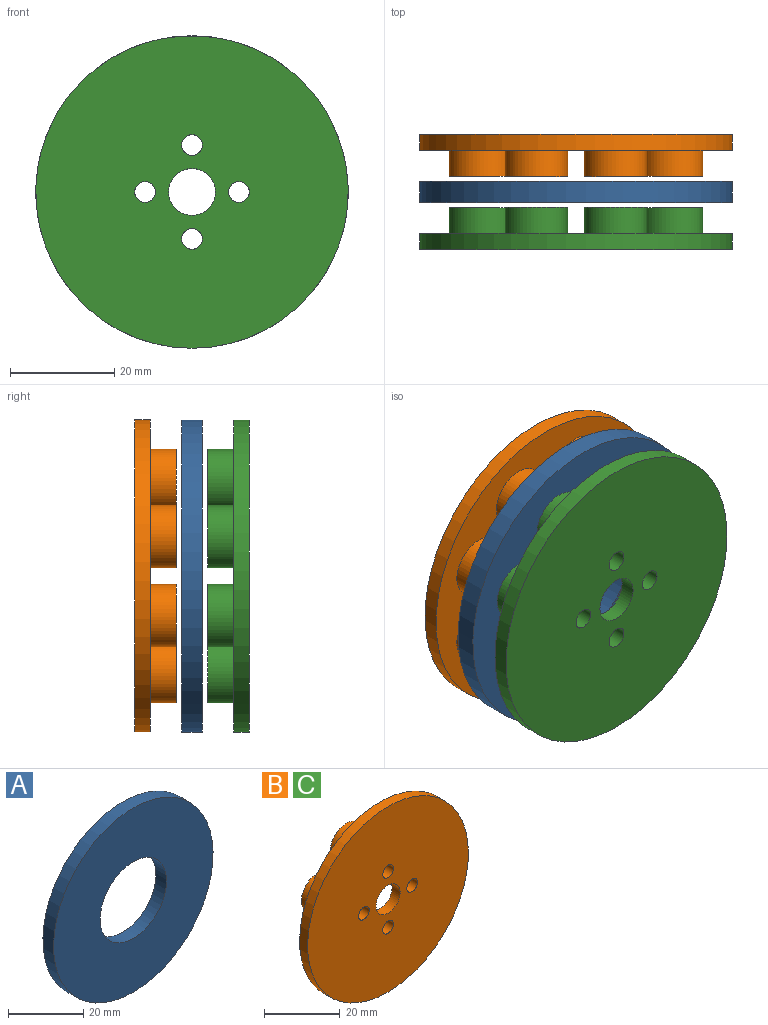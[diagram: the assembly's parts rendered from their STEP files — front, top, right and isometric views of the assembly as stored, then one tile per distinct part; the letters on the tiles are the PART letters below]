
ASSEMBLY  parts=3 mates=4
PART A: 4 faces, bbox 60x4x60 mm
  f0: cylinder r=12.5mm len=25mm, axis (0,1,0), area 314.2mm2, adj f2,f3
  f1: cylinder r=30mm len=60mm, axis (0,1,0), area 754mm2, adj f2,f3
  f2: plane 60x60mm, normal (0,-1,0), area 2336.6mm2, adj f0,f1
  f3: plane 60x60mm, normal (0,1,0), area 2336.6mm2, adj f0,f1
PART B: 24 faces, bbox 60x8x60 mm
  f0: cylinder r=30mm len=60mm, axis (0,1,0), area 565.5mm2, adj f1,f2
  f1: plane 60x60mm, normal (0,-1,0), area 2713.6mm2, adj f0,f3,f20,f21,f22,f23
  f2: plane 60x60mm, normal (0,1,0), area 1808.8mm2, adj f0,f3,f4,f6,f8,f10,f12,f14
  f3: cylinder r=4.5mm len=9mm, axis (0,-1,0), area 84.8mm2, adj f1,f2
  f4: cylinder r=6mm len=12mm, axis (0,-1,0), area 188.5mm2, adj f2,f5
  f5: plane 12x12mm, normal (0,1,0), area 113.1mm2, adj f4
  f6: cylinder r=6mm len=12mm, axis (0,-1,0), area 188.5mm2, adj f2,f7
  f7: plane 12x12mm, normal (0,1,0), area 113.1mm2, adj f6
  f8: cylinder r=6mm len=12mm, axis (0,-1,0), area 188.5mm2, adj f2,f9
  f9: plane 12x12mm, normal (0,1,0), area 113.1mm2, adj f8
  f10: cylinder r=6mm len=12mm, axis (0,-1,0), area 188.5mm2, adj f2,f11
  f11: plane 12x12mm, normal (0,1,0), area 113.1mm2, adj f10
  f12: cylinder r=6mm len=12mm, axis (0,-1,0), area 188.5mm2, adj f2,f13
  f13: plane 12x12mm, normal (0,1,0), area 113.1mm2, adj f12
  f14: cylinder r=6mm len=12mm, axis (0,-1,0), area 188.5mm2, adj f2,f15
  f15: plane 12x12mm, normal (0,1,0), area 113.1mm2, adj f14
  f16: cylinder r=6mm len=12mm, axis (0,-1,0), area 188.5mm2, adj f2,f17
  f17: plane 12x12mm, normal (0,1,0), area 113.1mm2, adj f16
  f18: cylinder r=6mm len=12mm, axis (0,-1,0), area 188.5mm2, adj f2,f19
  f19: plane 12x12mm, normal (0,1,0), area 113.1mm2, adj f18
  f20: cylinder r=2mm len=4mm, axis (0,1,0), area 37.7mm2, adj f1,f2
  f21: cylinder r=2mm len=4mm, axis (0,1,0), area 37.7mm2, adj f1,f2
  f22: cylinder r=2mm len=4mm, axis (0,1,0), area 37.7mm2, adj f1,f2
  f23: cylinder r=2mm len=4mm, axis (0,1,0), area 37.7mm2, adj f1,f2
PART C: same geometry as B
PLACE A t=(-0.17,2.33,-0.07)mm
PLACE B rot(axis=(1,0,0),180deg) t=(-0.17,8.33,-0.07)mm
PLACE C t=(-0.17,-7.67,-0.07)mm
MATE planar B.f14 <-> A.f1  axis (0,-1,0) through (-7.77,3.33,18.28)mm
MATE slider B.f3 <-> C.f3  axis (0,1,0) through (-0.17,9.83,-0.07)mm
MATE cylindrical C.f0 <-> A.f0  axis (0,-1,0) through (-0.17,-10.67,-0.07)mm
MATE planar C.f18 <-> A.f1  axis (0,-1,0) through (-18.52,-2.67,7.53)mm
